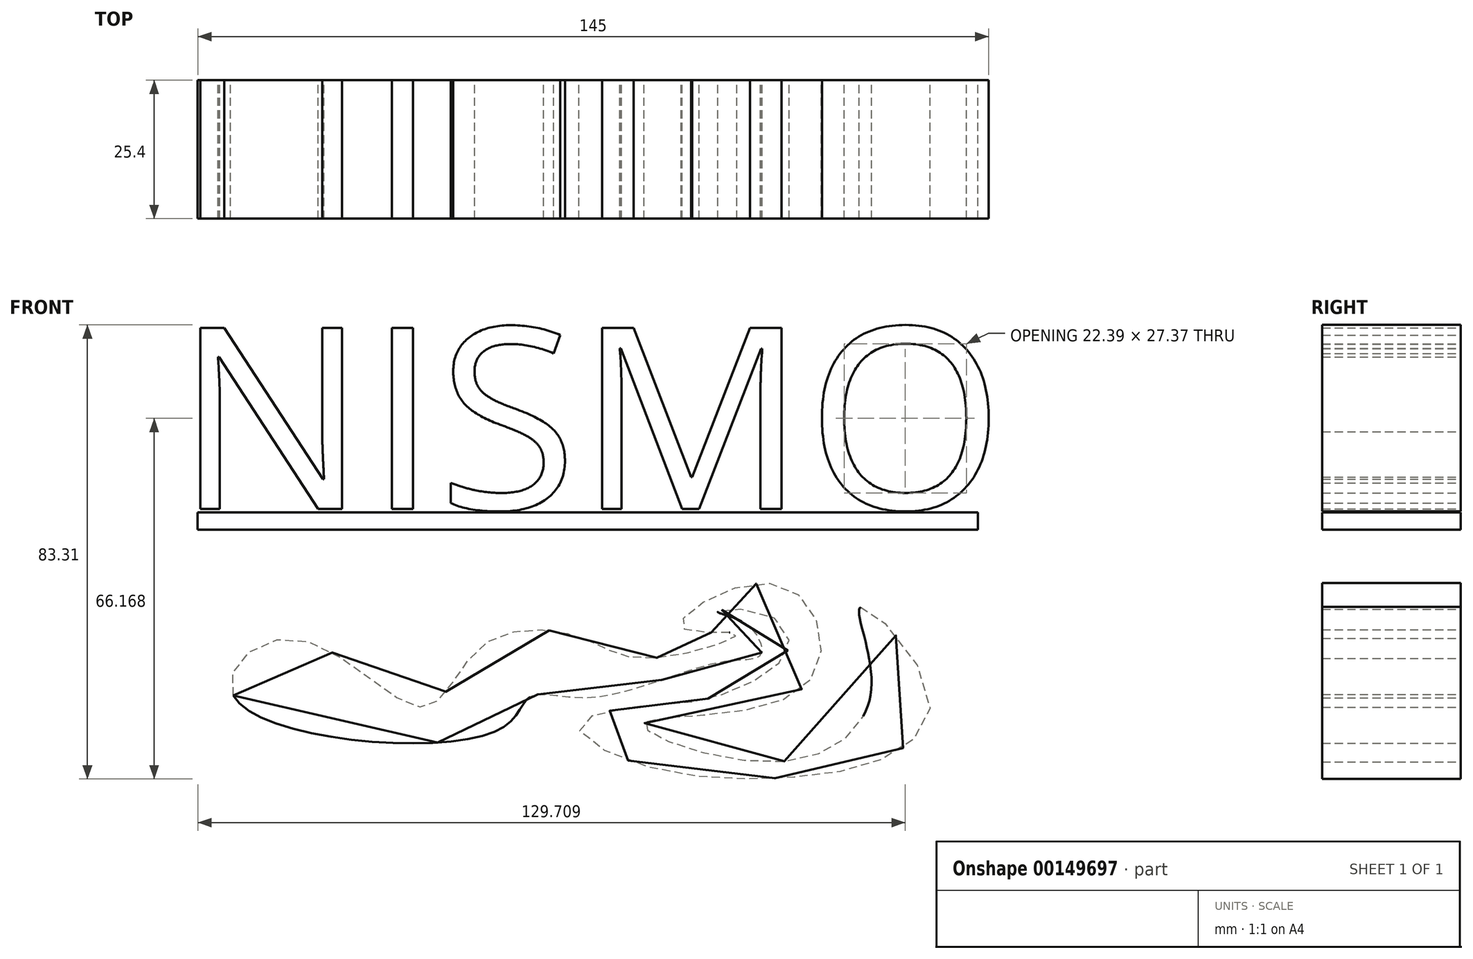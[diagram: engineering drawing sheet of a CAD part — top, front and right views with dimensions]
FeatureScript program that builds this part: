
annotation { "Feature Type Name" : "Feature", "Feature Type Description" : "" }
export const myFeature = defineFeature(function(context is Context, id is Id, definition is map)
    precondition{}
    {
        {
            var Q0;
            Q0=qCreatedBy(makeId("Front.planeOp"),FACE);
            var sketch = newSketch(context, id + "F0", { "sketchPlane" : qUnion([Q0])});
            skText(sketch, "E0", { "text": "NISMO", "fontName": "OpenSans-Regular.ttf"});
            const initialGuessF0  = {"E0": [-0.07606, -0.00453, 1, 0, 0.03352]};
            skSetInitialGuess(sketch, initialGuessF0);
            skSolve(sketch);
        }
        {
            var Q0;
            Q0=makeQuery(id+"F0.imprint","IMPRINT",FACE,{"disambiguationData":[TD([[makeQuery(id+"F0.imprint","IMPRINT",EDGE,{"derivedFrom":sQuery(id+"F0.wireOp",EDGE,"E0.sketch_text.stroke-0")}),-1.0]])]});
            extrude(context, id + "F1", {"entities" : qUnion([Q0]), "depth" : 25.4 * mm});
        }
        {
            var Q0;
            Q0=makeQuery(id+"F0.imprint","IMPRINT",FACE,{"disambiguationData":[TD([[makeQuery(id+"F0.imprint","IMPRINT",EDGE,{"derivedFrom":sQuery(id+"F0.wireOp",EDGE,"E0.sketch_text.stroke-15")}),-1.0]])]});
            extrude(context, id + "F2", {"entities" : qUnion([Q0]), "depth" : 25.4 * mm});
        }
        {
            var Q0;
            Q0=makeQuery(id+"F0.imprint","IMPRINT",FACE,{"disambiguationData":[TD([[makeQuery(id+"F0.imprint","IMPRINT",EDGE,{"derivedFrom":sQuery(id+"F0.wireOp",EDGE,"E0.sketch_text.stroke-19")}),-1.0]])]});
            extrude(context, id + "F3", {"entities" : qUnion([Q0]), "depth" : 25.4 * mm});
        }
        {
            var Q0;
            Q0=makeQuery(id+"F0.imprint","IMPRINT",FACE,{"disambiguationData":[TD([[makeQuery(id+"F0.imprint","IMPRINT",EDGE,{"derivedFrom":sQuery(id+"F0.wireOp",EDGE,"E0.sketch_text.stroke-44")}),-1.0]])]});
            extrude(context, id + "F4", {"entities" : qUnion([Q0]), "depth" : 25.4 * mm});
        }
        {
            var Q0;
            Q0=makeQuery(id+"F0.imprint","IMPRINT",FACE,{"disambiguationData":[TD([[makeQuery(id+"F0.imprint","IMPRINT",EDGE,{"derivedFrom":sQuery(id+"F0.wireOp",EDGE,"E0.sketch_text.stroke-62")}),-1.0]])]});
            extrude(context, id + "F5", {"entities" : qUnion([Q0]), "depth" : 25.4 * mm});
        }
        {
            var Q0;
            Q0=qCreatedBy(makeId("Front.planeOp"),FACE);
            var sketch = newSketch(context, id + "F6", { "sketchPlane" : qUnion([Q0])});
            skLineSegment(sketch, "E1.bottom", {"start": v(-71.98, -5.15) * mm, "end": v(71.05, -5.15) * mm});
            skLineSegment(sketch, "E1.top", {"start": v(-71.98, -8.35) * mm, "end": v(71.05, -8.35) * mm});
            skLineSegment(sketch, "E1.left", {"start": v(-71.98, -5.15) * mm, "end": v(-71.98, -8.35) * mm});
            skLineSegment(sketch, "E1.right", {"start": v(71.05, -5.15) * mm, "end": v(71.05, -8.35) * mm});
            skSolve(sketch);
        }
        {
            var Q0;
            Q0=makeQuery(id+"F6.imprint","IMPRINT",FACE,{"disambiguationData":[TD([[makeQuery(id+"F6.imprint","IMPRINT",EDGE,{"derivedFrom":sQuery(id+"F6.wireOp",EDGE,"E1.bottom")}),-1.0]])]});
            extrude(context, id + "F7", {"entities" : qUnion([Q0]), "depth" : 25.4 * mm});
        }
        {
            var Q0;
            Q0=qCreatedBy(makeId("Front.planeOp"),FACE);
            var sketch = newSketch(context, id + "F8", { "sketchPlane" : qUnion([Q0])});
            skFitSpline(sketch, "E2", {"points": [v(-65.45, -38.75) * mm, v(-54.78, -28.3) * mm, v(-30.66, -40.89) * mm, v(-19.77, -29.57) * mm, v(-1.84, -28.08) * mm, v(10.75, -31.92) * mm, v(26.76, -27.44) * mm, v(16.73, -26.16) * mm, v(34.66, -18.47) * mm, v(39.36, -37.05) * mm, v(9.9, -43.88) * mm, v(34.02, -50.92) * mm, v(51.53, -37.26) * mm, v(49.6, -22.53) * mm, v(61.99, -37.9) * mm, v(55.58, -49.43) * mm, v(34.88, -53.9) * mm, v(8.83, -51.35) * mm, v(-2.05, -44.3) * mm, v(9.05, -40.67) * mm, v(19.08, -39.82) * mm, v(29.75, -36.2) * mm, v(36.37, -29.79) * mm, v(32.32, -23.81) * mm, v(23.35, -23.38) * mm, v(28.69, -25.73) * mm, v(31.25, -31.28) * mm, v(24.42, -32.56) * mm, v(0, -39.18) * mm, v(-11.02, -38.97) * mm, v(-17.42, -45.37) * mm, v(-65.45, -38.75) * mm]});
            skSolve(sketch);
        }
        {
            var Q0;
            Q0=makeQuery(id+"F8.imprint","IMPRINT",FACE,{"disambiguationData":[TD([[makeQuery(id+"F8.imprint","IMPRINT",EDGE,{"derivedFrom":sQuery(id+"F8.wireOp",EDGE,"E2")}),-1.0]])]});
            extrude(context, id + "F9", {"entities" : qUnion([Q0]), "depth" : 25.4 * mm});
        }
    });
